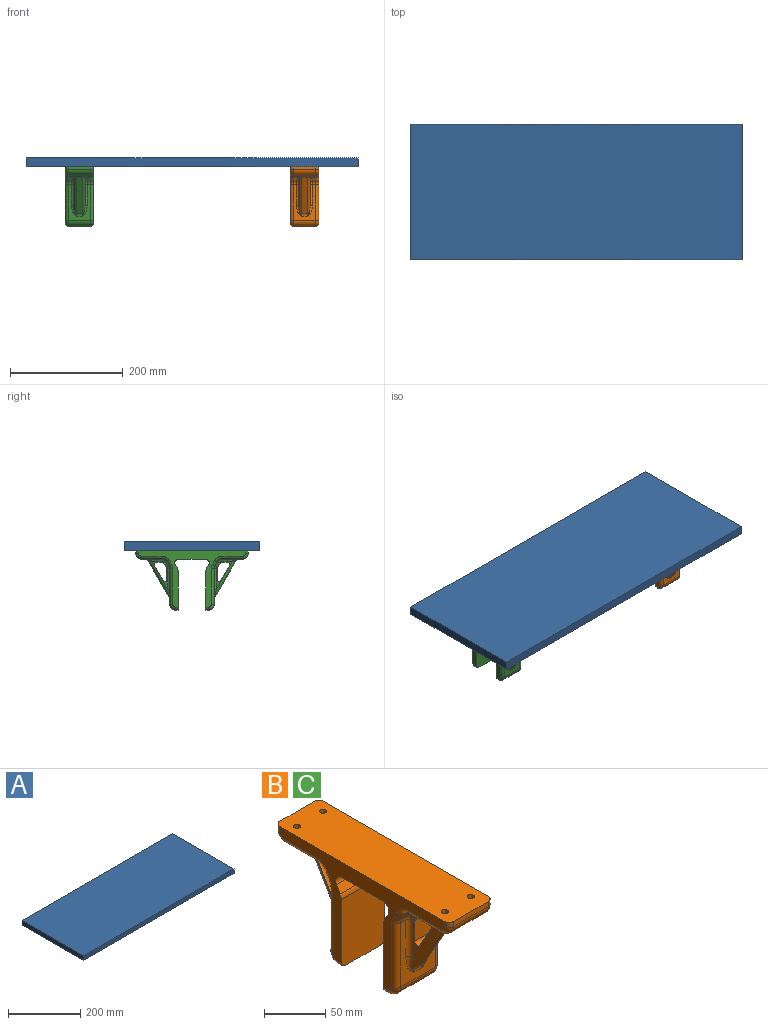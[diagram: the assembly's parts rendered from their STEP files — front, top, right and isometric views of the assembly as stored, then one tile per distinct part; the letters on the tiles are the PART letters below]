
ASSEMBLY  parts=3 mates=2
PART A: 6 faces, bbox 590x240x15.4 mm
  f0: plane 240x15.4mm, normal (-1,0,0), area 3696mm2, adj f1,f3,f4,f5
  f1: plane 590x15.4mm, normal (0,-1,0), area 9086mm2, adj f0,f2,f4,f5
  f2: plane 240x15.4mm, normal (1,0,0), area 3696mm2, adj f1,f3,f4,f5
  f3: plane 590x15.4mm, normal (0,1,0), area 9086mm2, adj f0,f2,f4,f5
  f4: plane 590x240mm, normal (0,0,1), area 141600mm2, adj f0,f1,f2,f3
  f5: plane 590x240mm, normal (0,0,-1), area 141600mm2, adj f0,f1,f2,f3
PART B: 150 faces, bbox 50.6x202.3x107.1 mm
  f0: plane 200x50mm, normal (0,0,1), area 9880mm2, adj f3,f6,f14,f15,f62,f71,f80,f89
  f1: plane 49.74x28.72mm, normal (1,0,0), area 215.9mm2, adj f32,f33,f34,f35,f40,f41,f42,f43
  f2: plane 49.74x28.72mm, normal (-1,0,0), area 215.9mm2, adj f32,f33,f34,f35,f40,f41,f42,f43
  f3: plane 190x100.67mm, normal (-1,0,0), area 3976.3mm2, adj f0,f7,f8,f9,f10,f19,f20,f21
  f4: plane 63.35x36.57mm, normal (0,0.87,-0.5), area 731.5mm2, adj f54,f55,f102,f105
  f5: plane 63.35x36.57mm, normal (0,-0.87,-0.5), area 731.5mm2, adj f58,f59,f99,f108
  f6: plane 190x100.67mm, normal (1,0,0), area 3976.3mm2, adj f0,f7,f8,f9,f10,f19,f20,f21
  f7: plane 50x7.18mm, normal (0,0.87,0.5), area 414.5mm2, adj f3,f6,f20,f61
  f8: plane 50x47.25mm, normal (0,0,-1), area 2362.3mm2, adj f3,f6,f20,f21
  f9: plane 50x7.18mm, normal (0,-0.87,0.5), area 414.5mm2, adj f3,f6,f21,f52
  f10: plane 67.99x50mm, normal (0,-1,0), area 3388.7mm2, adj f3,f6,f11,f52,f70,f88
  f11: plane 40x5mm, normal (0,0,-1), area 200mm2, adj f10,f53,f70,f88
  f12: plane 63.97x40mm, normal (0,1,0), area 1066.8mm2, adj f47,f49,f53,f54,f68,f86,f116,f117
  f13: plane 40.63x37.56mm, normal (0,0,-1), area 594.2mm2, adj f46,f48,f55,f56,f64,f82,f110,f111
  f14: plane 40x5mm, normal (0,1,0), area 200mm2, adj f0,f56,f62,f80
  f15: plane 40x5mm, normal (0,-1,0), area 200mm2, adj f0,f57,f71,f89
  f16: plane 40.63x37.56mm, normal (0,0,-1), area 594.2mm2, adj f44,f50,f57,f58,f73,f91,f128,f129
  f17: plane 63.97x40mm, normal (0,-1,0), area 1066.8mm2, adj f45,f51,f59,f60,f77,f95,f134,f135
  f18: plane 40x5mm, normal (0,0,-1), area 200mm2, adj f19,f60,f79,f97
  f19: plane 67.99x50mm, normal (0,1,0), area 3388.7mm2, adj f3,f6,f18,f61,f79,f97
  f20: cylinder r=7mm len=50mm, axis (-1,0,0), area 733mm2, adj f3,f6,f7,f8
  f21: cylinder r=7mm len=50mm, axis (1,0,0), area 733mm2, adj f3,f6,f8,f9
  f22: plane 6.7x6mm, normal (0,0.87,-0.5), area 46.4mm2, adj f48,f49,f66,f123
  f23: plane 49.74x28.72mm, normal (1,0,0), area 215.9mm2, adj f28,f29,f30,f31,f36,f37,f38,f39
  f24: plane 6.7x6mm, normal (0,-0.87,-0.5), area 46.4mm2, adj f50,f51,f75,f141
  f25: plane 6.7x6mm, normal (0,-0.87,-0.5), area 46.4mm2, adj f44,f45,f93,f132
  f26: plane 6.7x6mm, normal (0,0.87,-0.5), area 46.4mm2, adj f46,f47,f84,f114
  f27: plane 49.74x28.72mm, normal (-1,0,0), area 215.9mm2, adj f28,f29,f30,f31,f36,f37,f38,f39
  f28: plane 20x11.92mm, normal (0,0,-1), area 238.4mm2, adj f23,f27,f36,f39
  f29: plane 28.08x20mm, normal (0,-0.87,0.5), area 648.5mm2, adj f23,f27,f36,f37
  f30: plane 20.65x20mm, normal (0,1,0), area 413mm2, adj f23,f27,f37,f38
  f31: plane 20x7.43mm, normal (0,0.87,-0.5), area 171.6mm2, adj f23,f27,f38,f39
  f32: plane 20x11.92mm, normal (0,0,-1), area 238.4mm2, adj f1,f2,f40,f43
  f33: plane 20x7.43mm, normal (0,-0.87,-0.5), area 171.6mm2, adj f1,f2,f40,f41
  f34: plane 20.65x20mm, normal (0,-1,0), area 413mm2, adj f1,f2,f41,f42
  f35: plane 28.08x20mm, normal (0,0.87,0.5), area 648.5mm2, adj f1,f2,f42,f43
  f36: cylinder r=3mm len=20mm, axis (1,0,0), area 125.7mm2, adj f23,f27,f28,f29
  f37: cylinder r=3mm len=20mm, axis (1,0,0), area 157.1mm2, adj f23,f27,f29,f30
  f38: cylinder r=3mm len=20mm, axis (1,0,0), area 31.4mm2, adj f23,f27,f30,f31
  f39: cylinder r=3mm len=20mm, axis (1,0,0), area 62.8mm2, adj f23,f27,f28,f31
  f40: cylinder r=3mm len=20mm, axis (1,0,0), area 62.8mm2, adj f1,f2,f32,f33
  f41: cylinder r=3mm len=20mm, axis (1,0,0), area 31.4mm2, adj f1,f2,f33,f34
  f42: cylinder r=3mm len=20mm, axis (1,0,0), area 157.1mm2, adj f1,f2,f34,f35
  f43: cylinder r=3mm len=20mm, axis (1,0,0), area 125.7mm2, adj f1,f2,f32,f35
  f44: cylinder r=10mm len=8.66mm, axis (-1,0,0), area 62.8mm2, adj f16,f25,f92,f131
  f45: cylinder r=10mm len=6mm, axis (-1,0,0), area 31.4mm2, adj f17,f25,f94,f133
  f46: cylinder r=10mm len=8.66mm, axis (-1,0,0), area 62.8mm2, adj f13,f26,f83,f113
  f47: cylinder r=10mm len=6mm, axis (-1,0,0), area 31.4mm2, adj f12,f26,f85,f115
  f48: cylinder r=10mm len=8.66mm, axis (-1,0,0), area 62.8mm2, adj f13,f22,f65,f122
  f49: cylinder r=10mm len=6mm, axis (-1,0,0), area 31.4mm2, adj f12,f22,f67,f124
  f50: cylinder r=10mm len=8.66mm, axis (-1,0,0), area 62.8mm2, adj f16,f24,f74,f142
  f51: cylinder r=10mm len=6mm, axis (-1,0,0), area 31.4mm2, adj f17,f24,f76,f140
  f52: cylinder r=10mm len=50mm, axis (-1,0,0), area 261.8mm2, adj f3,f6,f9,f10
  f53: cylinder r=10mm len=40mm, axis (-1,0,0), area 628.3mm2, adj f11,f12,f69,f87
  f54: cylinder r=10mm len=10mm, axis (1,0,0), area 52.4mm2, adj f4,f12,f101,f104
  f55: cylinder r=10mm len=10mm, axis (1,0,0), area 104.7mm2, adj f4,f13,f103,f106
  f56: cylinder r=10mm len=40mm, axis (-1,0,0), area 628.3mm2, adj f13,f14,f63,f81
  f57: cylinder r=10mm len=40mm, axis (-1,0,0), area 628.3mm2, adj f15,f16,f72,f90
  f58: cylinder r=10mm len=10mm, axis (1,0,0), area 104.7mm2, adj f5,f16,f100,f109
  f59: cylinder r=10mm len=10mm, axis (1,0,0), area 52.4mm2, adj f5,f17,f98,f107
  f60: cylinder r=10mm len=40mm, axis (-1,0,0), area 628.3mm2, adj f17,f18,f78,f96
  f61: cylinder r=10mm len=50mm, axis (-1,0,0), area 261.8mm2, adj f3,f6,f7,f19
  f62: cylinder r=5mm len=5mm, axis (0,0,-1), area 39.3mm2, adj f0,f6,f14,f63
  f63: torus R=5mm, axis (1,0,0), area 101mm2, adj f6,f56,f62,f64
  f64: cylinder r=5mm len=36.93mm, axis (0,-1,0), area 290.1mm2, adj f6,f13,f63,f65
  f65: torus R=15mm, axis (1,0,0), area 97.2mm2, adj f6,f48,f64,f66
  f66: cylinder r=5mm len=9.2mm, axis (0,0.5,0.87), area 60.8mm2, adj f6,f22,f65,f67
  f67: torus R=15mm, axis (1,0,0), area 48.6mm2, adj f6,f49,f66,f68
  f68: cylinder r=5mm len=63.97mm, axis (0,0,-1), area 502.4mm2, adj f6,f12,f67,f69
  f69: torus R=5mm, axis (1,0,0), area 101mm2, adj f6,f53,f68,f70
  f70: cylinder r=5mm len=5mm, axis (0,-1,0), area 39.3mm2, adj f6,f10,f11,f69
  f71: cylinder r=5mm len=5mm, axis (0,0,1), area 39.3mm2, adj f0,f6,f15,f72
  f72: torus R=5mm, axis (1,0,0), area 101mm2, adj f6,f57,f71,f73
  f73: cylinder r=5mm len=36.93mm, axis (0,-1,0), area 290.1mm2, adj f6,f16,f72,f74
  f74: torus R=15mm, axis (1,0,0), area 97.2mm2, adj f6,f50,f73,f75
  f75: cylinder r=5mm len=9.2mm, axis (0,0.5,-0.87), area 60.8mm2, adj f6,f24,f74,f76
  f76: torus R=15mm, axis (1,0,0), area 48.6mm2, adj f6,f51,f75,f77
  f77: cylinder r=5mm len=63.97mm, axis (0,0,1), area 502.4mm2, adj f6,f17,f76,f78
  f78: torus R=5mm, axis (1,0,0), area 101mm2, adj f6,f60,f77,f79
  f79: cylinder r=5mm len=5mm, axis (0,-1,0), area 39.3mm2, adj f6,f18,f19,f78
  f80: cylinder r=5mm len=5mm, axis (0,0,1), area 39.3mm2, adj f0,f3,f14,f81
  f81: torus R=5mm, axis (1,0,0), area 101mm2, adj f3,f56,f80,f82
  f82: cylinder r=5mm len=36.93mm, axis (0,1,0), area 290.1mm2, adj f3,f13,f81,f83
  f83: torus R=15mm, axis (1,0,0), area 97.2mm2, adj f3,f46,f82,f84
  f84: cylinder r=5mm len=9.2mm, axis (0,0.5,0.87), area 60.8mm2, adj f3,f26,f83,f85
  f85: torus R=15mm, axis (1,0,0), area 48.6mm2, adj f3,f47,f84,f86
  f86: cylinder r=5mm len=63.97mm, axis (0,0,1), area 502.4mm2, adj f3,f12,f85,f87
  f87: torus R=5mm, axis (1,0,0), area 101mm2, adj f3,f53,f86,f88
  f88: cylinder r=5mm len=5mm, axis (0,1,0), area 39.3mm2, adj f3,f10,f11,f87
  f89: cylinder r=5mm len=5mm, axis (0,0,-1), area 39.3mm2, adj f0,f3,f15,f90
  f90: torus R=5mm, axis (1,0,0), area 101mm2, adj f3,f57,f89,f91
  f91: cylinder r=5mm len=36.93mm, axis (0,1,0), area 290.1mm2, adj f3,f16,f90,f92
  f92: torus R=15mm, axis (1,0,0), area 97.2mm2, adj f3,f44,f91,f93
  f93: cylinder r=5mm len=9.2mm, axis (0,0.5,-0.87), area 60.8mm2, adj f3,f25,f92,f94
  f94: torus R=15mm, axis (1,0,0), area 48.6mm2, adj f3,f45,f93,f95
  f95: cylinder r=5mm len=63.97mm, axis (0,0,-1), area 502.4mm2, adj f3,f17,f94,f96
  f96: torus R=5mm, axis (1,0,0), area 101mm2, adj f3,f60,f95,f97
  f97: cylinder r=5mm len=5mm, axis (0,1,0), area 39.3mm2, adj f3,f18,f19,f96
  f98: torus R=15mm, axis (1,0,0), area 6mm2, adj f59,f99,f137
  f99: cylinder r=5mm len=65.85mm, axis (0,-0.5,0.87), area 538.7mm2, adj f1,f5,f98,f100,f138,f144
  f100: torus R=15mm, axis (1,0,0), area 27.7mm2, adj f58,f99,f145
  f101: torus R=15mm, axis (1,0,0), area 6mm2, adj f54,f102,f127
  f102: cylinder r=5mm len=65.85mm, axis (0,-0.5,-0.87), area 538.7mm2, adj f4,f23,f101,f103,f120,f126
  f103: torus R=15mm, axis (1,0,0), area 27.7mm2, adj f55,f102,f119
  f104: torus R=15mm, axis (-1,0,0), area 6mm2, adj f54,f105,f118
  f105: cylinder r=5mm len=65.85mm, axis (0,-0.5,-0.87), area 538.7mm2, adj f4,f27,f104,f106,f111,f117
  f106: torus R=15mm, axis (-1,0,0), area 27.7mm2, adj f55,f105,f110
  f107: torus R=15mm, axis (-1,0,0), area 6mm2, adj f59,f108,f136
  f108: cylinder r=5mm len=65.85mm, axis (0,-0.5,0.87), area 538.7mm2, adj f2,f5,f107,f109,f129,f135
  f109: torus R=15mm, axis (-1,0,0), area 27.7mm2, adj f58,f108,f128
  f110: bspline ~12.06x8.7mm, area 36mm2, adj f13,f106,f111
  f111: bspline ~6.2x4.46mm, area 16.6mm2, adj f13,f105,f110,f112
  f112: cylinder r=4mm len=18.85mm, axis (0,-1,0), area 118.4mm2, adj f13,f27,f111,f113
  f113: torus R=6mm, axis (-1,0,0), area 56.2mm2, adj f27,f46,f112,f114
  f114: cylinder r=4mm len=8.7mm, axis (0,0.5,0.87), area 48.6mm2, adj f26,f27,f113,f115
  f115: torus R=6mm, axis (-1,0,0), area 28.1mm2, adj f27,f47,f114,f116
  f116: cylinder r=4mm len=37.04mm, axis (0,0,-1), area 232.7mm2, adj f12,f27,f115,f117
  f117: bspline ~20.06x7.29mm, area 72.4mm2, adj f12,f105,f116,f118
  f118: bspline ~5.26x3.98mm, area 7.2mm2, adj f12,f104,f117
  f119: bspline ~12.7x8.88mm, area 38.8mm2, adj f13,f103,f120
  f120: bspline ~6.2x4.46mm, area 16.6mm2, adj f13,f102,f119,f121
  f121: cylinder r=4mm len=18.85mm, axis (0,-1,0), area 118.4mm2, adj f13,f23,f120,f122
  f122: torus R=6mm, axis (1,0,0), area 56.2mm2, adj f23,f48,f121,f123
  f123: cylinder r=4mm len=8.7mm, axis (0,-0.5,-0.87), area 48.6mm2, adj f22,f23,f122,f124
  f124: torus R=6mm, axis (1,0,0), area 28.1mm2, adj f23,f49,f123,f125
  f125: cylinder r=4mm len=37.04mm, axis (0,0,-1), area 232.7mm2, adj f12,f23,f124,f126
  f126: bspline ~20.06x7.29mm, area 72.4mm2, adj f12,f102,f125,f127
  f127: bspline ~5.26x3.98mm, area 7.2mm2, adj f12,f101,f126
  f128: bspline ~12.06x8.7mm, area 36mm2, adj f16,f109,f129
  f129: bspline ~6.2x4.46mm, area 16.6mm2, adj f16,f108,f128,f130
  f130: cylinder r=4mm len=18.85mm, axis (0,-1,0), area 118.4mm2, adj f2,f16,f129,f131
  f131: torus R=6mm, axis (-1,0,0), area 56.2mm2, adj f2,f44,f130,f132
  f132: cylinder r=4mm len=8.7mm, axis (0,0.5,-0.87), area 48.6mm2, adj f2,f25,f131,f133
  f133: torus R=6mm, axis (-1,0,0), area 28.1mm2, adj f2,f45,f132,f134
  f134: cylinder r=4mm len=37.04mm, axis (0,0,1), area 232.7mm2, adj f2,f17,f133,f135
  f135: bspline ~16.14x6.79mm, area 72.4mm2, adj f17,f108,f134,f136
  f136: bspline ~5.26x3.98mm, area 7.2mm2, adj f17,f107,f135
  f137: bspline ~5.26x3.98mm, area 7.2mm2, adj f17,f98,f138
  f138: bspline ~20.06x7.29mm, area 72.4mm2, adj f17,f99,f137,f139
  f139: cylinder r=4mm len=37.04mm, axis (0,0,1), area 232.7mm2, adj f1,f17,f138,f140
  f140: torus R=6mm, axis (1,0,0), area 28.1mm2, adj f1,f51,f139,f141
  f141: cylinder r=4mm len=8.7mm, axis (0,-0.5,0.87), area 48.6mm2, adj f1,f24,f140,f142
  f142: torus R=6mm, axis (1,0,0), area 56.2mm2, adj f1,f50,f141,f143
  f143: cylinder r=4mm len=18.85mm, axis (0,-1,0), area 118.4mm2, adj f1,f16,f142,f144
  f144: bspline ~4.29x4mm, area 16.6mm2, adj f16,f99,f143,f145
  f145: bspline ~12.7x8.88mm, area 38.8mm2, adj f16,f100,f144
  f146: cylinder r=2.8mm len=15mm, axis (0,0,1), area 263.9mm2, adj f0,f16
  f147: cylinder r=2.8mm len=15mm, axis (0,0,1), area 263.9mm2, adj f0,f16
  f148: cylinder r=2.8mm len=15mm, axis (0,0,1), area 263.9mm2, adj f0,f13
  f149: cylinder r=2.8mm len=15mm, axis (0,0,1), area 263.9mm2, adj f0,f13
PART C: same geometry as B
PLACE A at identity
PLACE B t=(470,120,0)mm
PLACE C t=(70,120,0)mm
MATE fastened B.f0 <-> A.f5  axis (0,0,1) through (495,20,0)mm
MATE fastened A.f5 <-> C.f0  axis (0,0,-1) through (295,0,0)mm
